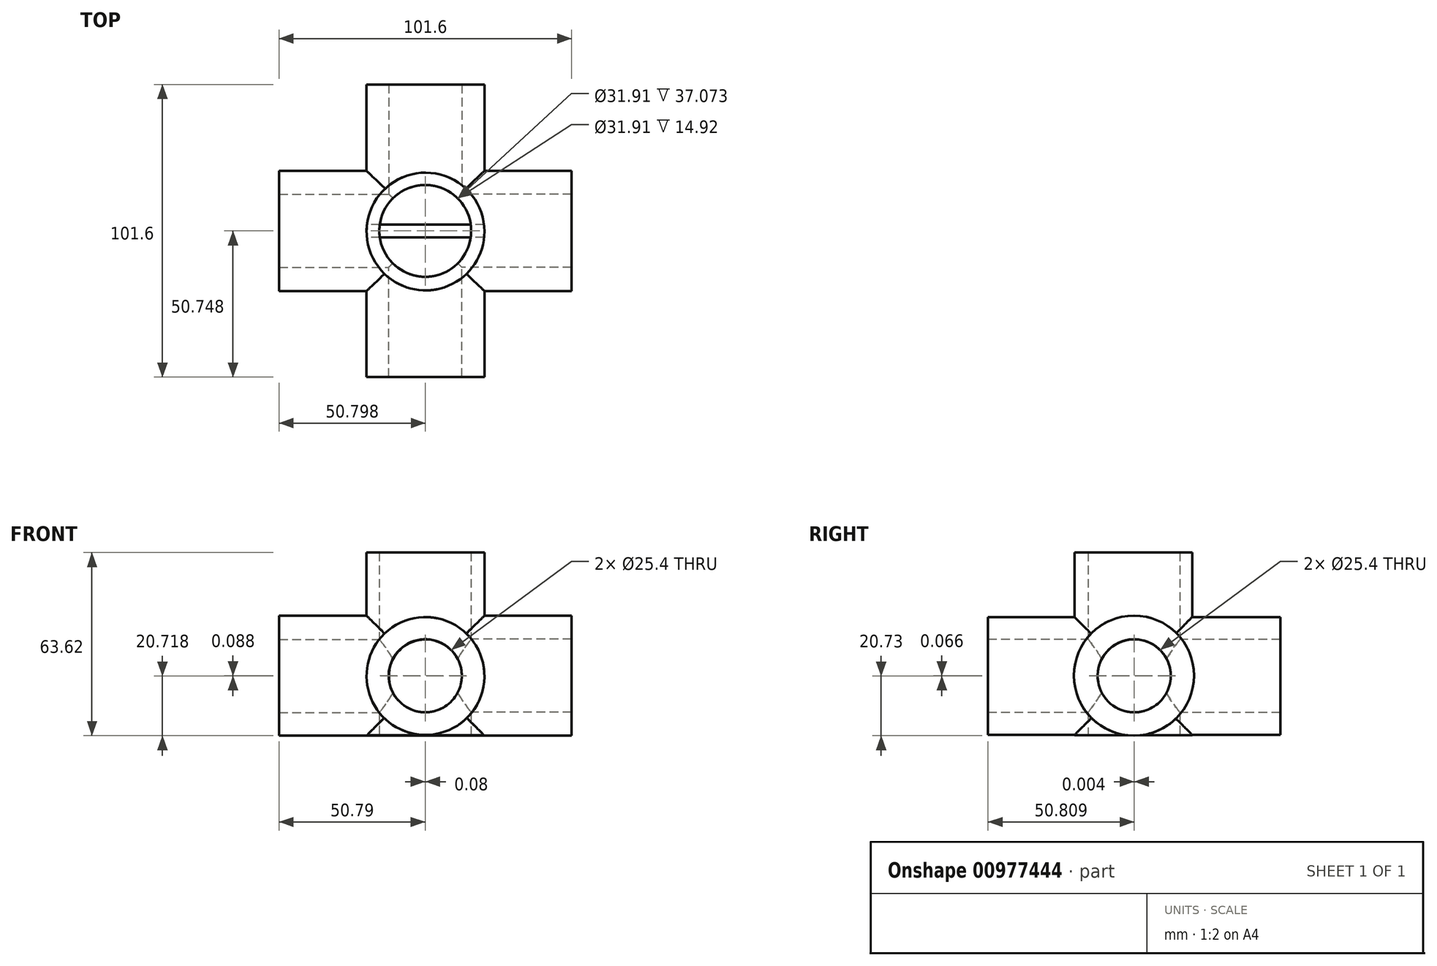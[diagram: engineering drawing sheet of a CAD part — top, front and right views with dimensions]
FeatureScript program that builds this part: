
annotation { "Feature Type Name" : "Feature", "Feature Type Description" : "" }
export const myFeature = defineFeature(function(context is Context, id is Id, definition is map)
    precondition{}
    {
        {
            var Q0;
            Q0=qCreatedBy(makeId("Front.planeOp"),FACE);
            var sketch = newSketch(context, id + "F0", { "sketchPlane" : qUnion([Q0])});
            skCircle(sketch, "E0", {"center": v(0.07, 20.6) * mm, "radius": 20.47 * mm});
            skSolve(sketch);
        }
        {
            var Q0;
            Q0=qSketchRegion(id+"F0",true);
            extrude(context, id + "F1", {"entities" : qUnion([Q0]), "depth" : 50.8 * mm, "offsetDistance" : 25.4 * mm, "hasSecondDirection" : true, "secondDirectionOppositeDirection" : true, "secondDirectionDepth" : 50.8 * mm});
        }
        {
            var Q0;
            Q0=qCreatedBy(makeId("Top.planeOp"),FACE);
            var sketch = newSketch(context, id + "F2", { "sketchPlane" : qUnion([Q0])});
            skCircle(sketch, "E1", {"center": v(0.07, -0.28) * mm, "radius": 20.46 * mm});
            skSolve(sketch);
        }
        {
            var Q0;
            Q0=qSketchRegion(id+"F2",true);
            extrude(context, id + "F3", {"entities" : qUnion([Q0]), "operationType" : NewBodyOperationType.ADD, "depth" : 63.5 * mm, "offsetDistance" : 25.4 * mm});
        }
        {
            var Q0;
            Q0=qCreatedBy(makeId("Right.planeOp"),FACE);
            var sketch = newSketch(context, id + "F4", { "sketchPlane" : qUnion([Q0])});
            skCircle(sketch, "E2", {"center": v(-0.07, 20.74) * mm, "radius": 20.86 * mm});
            skSolve(sketch);
        }
        {
            var Q0;
            Q0=qSketchRegion(id+"F4",true);
            extrude(context, id + "F5", {"entities" : qUnion([Q0]), "operationType" : NewBodyOperationType.ADD, "depth" : 50.8 * mm, "offsetDistance" : 25.4 * mm, "hasSecondDirection" : true, "secondDirectionOppositeDirection" : true, "secondDirectionDepth" : 50.8 * mm});
        }
        {
            var Q0;
            Q0=qCreatedBy(makeId("Right.planeOp"),FACE);
            var sketch = newSketch(context, id + "F6", { "sketchPlane" : qUnion([Q0])});
            skPoint(sketch, "E3", {"position": v(0, 20.61) * mm});
            skSolve(sketch);
        }
        {
            var Q0;
            Q0=sQuery(id+"F6.wireOp",VERTEX,"E3");
            var Q1;
            Q1=makeQuery(id+"F1.opExtrude","SWEPT_BODY",BODY,{"disambiguationData":[OSD([sQuery(id+"F0.wireOp",EDGE,"E0")])]});
            hole(context, id + "F7", {"style" : HoleStyle.SIMPLE, "endStyle" : HoleEndStyle.THROUGH, "holeDiameter" : 25.4 * mm, "majorDiameter" : 6.35 * mm, "isTappedThrough" : true, "tappedDepth" : 12.7 * mm, "tapClearance" : 3, "locations" : qUnion([Q0]), "scope" : qUnion([Q1])});
        }
        {
            var Q0;
            Q0=qCreatedBy(makeId("Right.planeOp"),FACE);
            var sketch = newSketch(context, id + "F8", { "sketchPlane" : qUnion([Q0])});
            skPoint(sketch, "E4", {"position": v(0.01, 20.68) * mm});
            skSolve(sketch);
        }
        {
            var Q0;
            Q0=sQuery(id+"F0.wireOp",VERTEX,"E0.center");
            var Q1;
            Q1=makeQuery(id+"F1.opExtrude","SWEPT_BODY",BODY,{"disambiguationData":[OSD([sQuery(id+"F0.wireOp",EDGE,"E0")])]});
            hole(context, id + "F9", {"style" : HoleStyle.SIMPLE, "endStyle" : HoleEndStyle.THROUGH, "holeDiameter" : 25.4 * mm, "majorDiameter" : 6.35 * mm, "isTappedThrough" : true, "tappedDepth" : 12.7 * mm, "tapClearance" : 3, "locations" : qUnion([Q0]), "scope" : qUnion([Q1])});
        }
        {
            var Q0;
            Q0=sQuery(id+"F8.wireOp",VERTEX,"E4");
            var Q1;
            Q1=makeQuery(id+"F1.opExtrude","SWEPT_BODY",BODY,{"disambiguationData":[OSD([sQuery(id+"F0.wireOp",EDGE,"E0")])]});
            hole(context, id + "F10", {"style" : HoleStyle.SIMPLE, "endStyle" : HoleEndStyle.THROUGH, "oppositeDirection" : true, "holeDiameter" : 25.4 * mm, "majorDiameter" : 6.35 * mm, "isTappedThrough" : true, "tappedDepth" : 12.7 * mm, "tapClearance" : 3, "locations" : qUnion([Q0]), "scope" : qUnion([Q1])});
        }
        {
            var Q0;
            Q0=qCreatedBy(makeId("Front.planeOp"),FACE);
            var sketch = newSketch(context, id + "F11", { "sketchPlane" : qUnion([Q0])});
            skPoint(sketch, "E5", {"position": v(-0.01, 20.69) * mm});
            skSolve(sketch);
        }
        {
            var Q0;
            Q0=sQuery(id+"F11.wireOp",VERTEX,"E5");
            var Q1;
            Q1=makeQuery(id+"F1.opExtrude","SWEPT_BODY",BODY,{"disambiguationData":[OSD([sQuery(id+"F0.wireOp",EDGE,"E0")])]});
            hole(context, id + "F12", {"style" : HoleStyle.SIMPLE, "endStyle" : HoleEndStyle.THROUGH, "oppositeDirection" : true, "holeDiameter" : 25.4 * mm, "majorDiameter" : 6.35 * mm, "isTappedThrough" : true, "tappedDepth" : 12.7 * mm, "tapClearance" : 3, "locations" : qUnion([Q0]), "scope" : qUnion([Q1])});
        }
        {
            var Q0;
            Q0=qCreatedBy(makeId("Top.planeOp"),FACE);
            var sketch = newSketch(context, id + "F13", { "sketchPlane" : qUnion([Q0])});
            skPoint(sketch, "E6", {"position": v(0, -0.05) * mm});
            skCircle(sketch, "E7", {"center": v(0, -0.05) * mm, "radius": 15.95 * mm});
            skSolve(sketch);
        }
        {
            var Q0;
            Q0=qSketchRegion(id+"F13",true);
            extrude(context, id + "F14", {"entities" : qUnion([Q0]), "operationType" : NewBodyOperationType.REMOVE, "depth" : 84.58 * mm, "offsetDistance" : 25.4 * mm});
        }
    });
